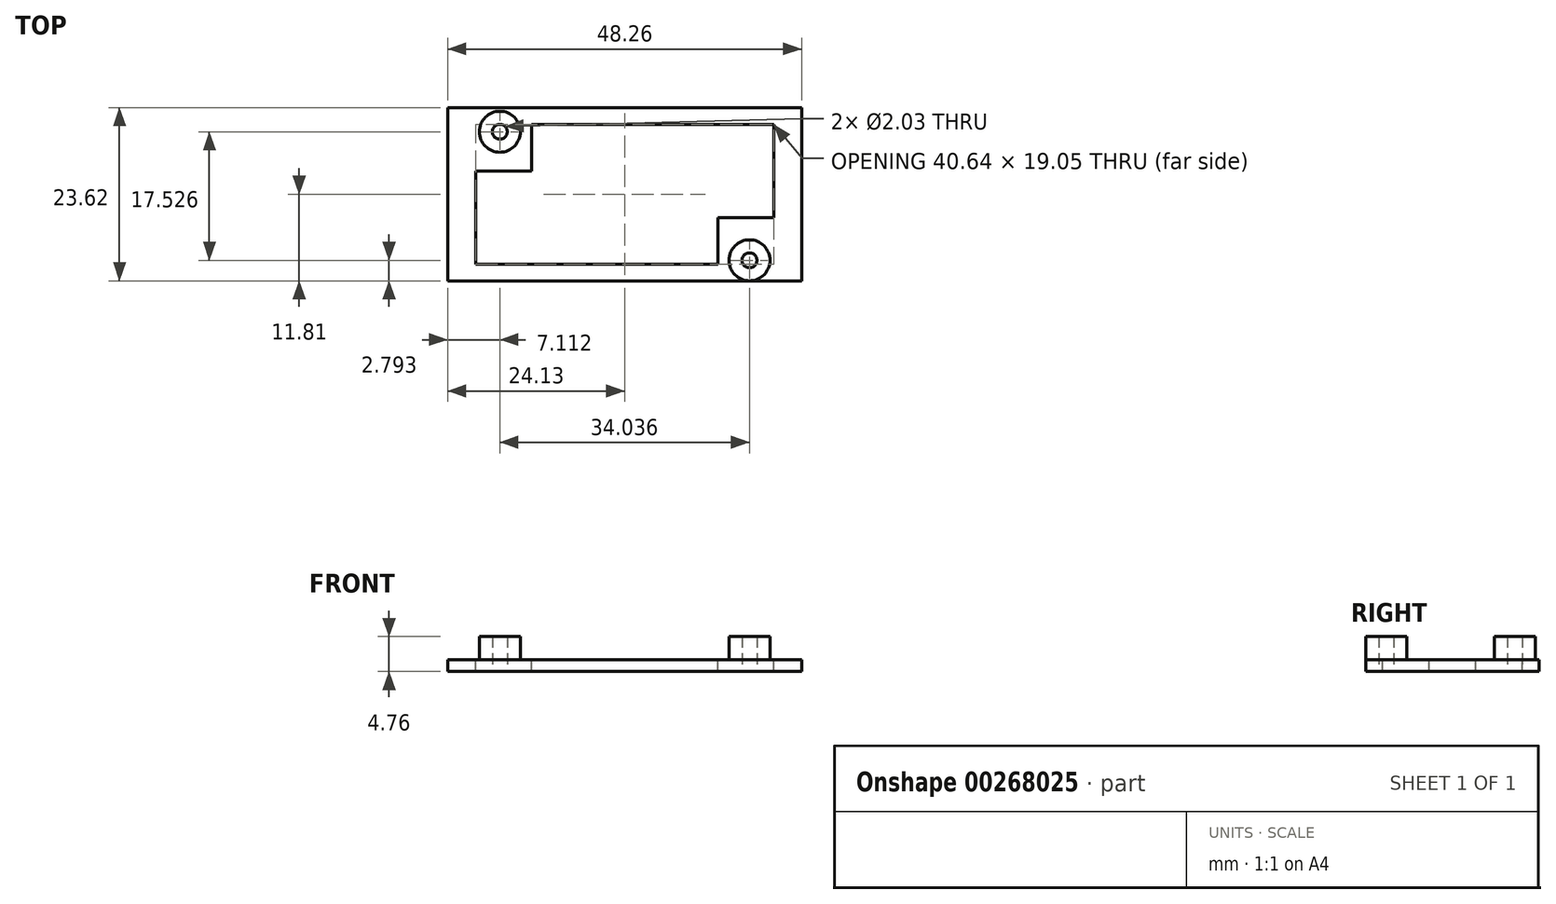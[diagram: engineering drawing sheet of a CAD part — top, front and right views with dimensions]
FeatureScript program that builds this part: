
annotation { "Feature Type Name" : "Feature", "Feature Type Description" : "" }
export const myFeature = defineFeature(function(context is Context, id is Id, definition is map)
    precondition{}
    {
        {
            var Q0;
            Q0=qCreatedBy(makeId("Top.planeOp"),FACE);
            var sketch = newSketch(context, id + "F0", { "sketchPlane" : qUnion([Q0])});
            skLineSegment(sketch, "E0.bottom", {"start": v(24.13, 11.81) * mm, "end": v(-24.13, 11.81) * mm});
            skLineSegment(sketch, "E0.top", {"start": v(24.13, -11.81) * mm, "end": v(-24.13, -11.81) * mm});
            skLineSegment(sketch, "E0.left", {"start": v(24.13, 11.81) * mm, "end": v(24.13, -11.81) * mm});
            skLineSegment(sketch, "E0.right", {"start": v(-24.13, 11.81) * mm, "end": v(-24.13, -11.81) * mm});
            skPoint(sketch, "E0.middle", {"position": v(0, 0) * mm});
            skSolve(sketch);
        }
        {
            var Q0;
            Q0=makeQuery(id+"F0.imprint","IMPRINT",FACE,{"disambiguationData":[TD([[makeQuery(id+"F0.imprint","IMPRINT",EDGE,{"derivedFrom":sQuery(id+"F0.wireOp",EDGE,"E0.bottom")}),1.0]])]});
            extrude(context, id + "F1", {"entities" : qUnion([Q0]), "depth" : 1.59 * mm});
        }
        {
            var Q0;
            Q0=makeQuery(id+"F1.opExtrude","CAP_FACE",FACE,{"disambiguationData":[OSD([sQuery(id+"F0.wireOp",EDGE,"E0.bottom"),sQuery(id+"F0.wireOp",EDGE,"E0.top"),sQuery(id+"F0.wireOp",EDGE,"E0.left"),sQuery(id+"F0.wireOp",EDGE,"E0.right")])],"isStart":false});
            var sketch = newSketch(context, id + "F2", { "sketchPlane" : qUnion([Q0])});
            skLineSegment(sketch, "E1.bottom", {"start": v(17.02, -11.81) * mm, "end": v(24.13, -11.81) * mm, "construction": true});
            skLineSegment(sketch, "E1.top", {"start": v(17.02, -9.02) * mm, "end": v(24.13, -9.02) * mm, "construction": true});
            skLineSegment(sketch, "E1.left", {"start": v(17.02, -11.81) * mm, "end": v(17.02, -9.02) * mm, "construction": true});
            skLineSegment(sketch, "E1.right", {"start": v(24.13, -11.81) * mm, "end": v(24.13, -9.02) * mm, "construction": true});
            skCircle(sketch, "E2", {"center": v(17.02, -9.02) * mm, "radius": 1.02 * mm});
            skCircle(sketch, "E3", {"center": v(17.02, -9.02) * mm, "radius": 2.8 * mm});
            skLineSegment(sketch, "E4.bottom", {"start": v(17.02, -9.02) * mm, "end": v(-17.02, -9.02) * mm, "construction": true});
            skLineSegment(sketch, "E4.top", {"start": v(17.02, 8.5) * mm, "end": v(-17.02, 8.5) * mm, "construction": true});
            skLineSegment(sketch, "E4.left", {"start": v(17.02, -9.02) * mm, "end": v(17.02, 8.5) * mm, "construction": true});
            skLineSegment(sketch, "E4.right", {"start": v(-17.02, -9.02) * mm, "end": v(-17.02, 8.5) * mm, "construction": true});
            skCircle(sketch, "E5", {"center": v(-17.02, 8.5) * mm, "radius": 1.02 * mm});
            skCircle(sketch, "E6", {"center": v(-17.02, 8.5) * mm, "radius": 2.8 * mm});
            skLineSegment(sketch, "E7.bottom", {"start": v(24.13, -11.81) * mm, "end": v(-24.13, -11.81) * mm, "construction": true});
            skLineSegment(sketch, "E7.top", {"start": v(24.13, 11.81) * mm, "end": v(-24.13, 11.81) * mm, "construction": true});
            skLineSegment(sketch, "E7.left", {"start": v(24.13, -11.81) * mm, "end": v(24.13, 11.81) * mm, "construction": true});
            skLineSegment(sketch, "E7.right", {"start": v(-24.13, -11.81) * mm, "end": v(-24.13, 11.81) * mm, "construction": true});
            skLineSegment(sketch, "E8.top", {"start": v(24.13, 11.3) * mm, "end": v(-24.13, 11.3) * mm, "construction": true});
            skLineSegment(sketch, "E8.left", {"start": v(24.13, -11.81) * mm, "end": v(24.13, 11.3) * mm, "construction": true});
            skLineSegment(sketch, "E8.right", {"start": v(-24.13, -11.81) * mm, "end": v(-24.13, 11.3) * mm, "construction": true});
            skLineSegment(sketch, "E9.bottom", {"start": v(-17.02, 8.5) * mm, "end": v(-24.13, 8.5) * mm, "construction": true});
            skLineSegment(sketch, "E9.top", {"start": v(-17.02, 11.3) * mm, "end": v(-24.13, 11.3) * mm, "construction": true});
            skLineSegment(sketch, "E9.left", {"start": v(-17.02, 8.5) * mm, "end": v(-17.02, 11.3) * mm, "construction": true});
            skLineSegment(sketch, "E9.right", {"start": v(-24.13, 8.5) * mm, "end": v(-24.13, 11.3) * mm, "construction": true});
            skSolve(sketch);
        }
        {
            var Q0;
            Q0=makeQuery(id+"F2.imprint","IMPRINT",FACE,{"disambiguationData":[TD([[makeQuery(id+"F2.imprint","IMPRINT",EDGE,{"derivedFrom":sQuery(id+"F2.wireOp",EDGE,"E5")}),-1.0]])]});
            var Q1;
            Q1 = qSketchRegion(id + "F2", true);
            var Q2;
            Q2=makeQuery(id+"F2.imprint","IMPRINT",FACE,{"disambiguationData":[TD([[makeQuery(id+"F2.imprint","IMPRINT",EDGE,{"derivedFrom":sQuery(id+"F2.wireOp",EDGE,"E2")}),-1.0]])]});
            extrude(context, id + "F3", {"entities" : qUnion([Q0, Q1, Q2]), "operationType" : NewBodyOperationType.ADD, "depth" : 3.17 * mm});
        }
        {
            var Q0;
            Q0=makeQuery(id+"F2.imprint","IMPRINT",FACE,{"disambiguationData":[TD([[makeQuery(id+"F2.imprint","IMPRINT",EDGE,{"derivedFrom":sQuery(id+"F2.wireOp",EDGE,"E5")}),1.0]])]});
            var Q1;
            Q1=makeQuery(id+"F2.imprint","IMPRINT",FACE,{"disambiguationData":[TD([[makeQuery(id+"F2.imprint","IMPRINT",EDGE,{"derivedFrom":sQuery(id+"F2.wireOp",EDGE,"E2")}),1.0]])]});
            extrude(context, id + "F4", {"entities" : qUnion([Q0, Q1]), "operationType" : NewBodyOperationType.REMOVE, "oppositeDirection" : true, "depth" : 6.35 * mm});
        }
        {
            var Q0;
            {var subQ0=sQuery(id+"F0.wireOp",EDGE,"E0.left");var subQ1=sQuery(id+"F0.wireOp",EDGE,"E0.top");var subQ2=sQuery(id+"F0.wireOp",EDGE,"E0.right");var subQ3=sQuery(id+"F0.wireOp",EDGE,"E0.bottom");Q0=makeQuery(id+"F3.boolean.opBoolean","SPLIT",FACE,{"disambiguationData":[TD([makeQuery(id+"F1.opExtrude","SWEPT_FACE",FACE,{"disambiguationData":[OSD([subQ3])]})])],"derivedFrom":makeQuery(id+"F1.opExtrude","CAP_FACE",FACE,{"disambiguationData":[OSD([subQ3,subQ1,subQ0,subQ2])],"isStart":false})});}
            var sketch = newSketch(context, id + "F5", { "sketchPlane" : qUnion([Q0])});
            skLineSegment(sketch, "E10.bottom", {"start": v(12.7, -9.52) * mm, "end": v(-12.7, -9.53) * mm});
            skLineSegment(sketch, "E10.top", {"start": v(12.7, 9.53) * mm, "end": v(-12.7, 9.52) * mm});
            skLineSegment(sketch, "E10.left", {"start": v(12.7, -9.53) * mm, "end": v(12.7, 9.53) * mm});
            skLineSegment(sketch, "E10.right", {"start": v(-12.7, -9.53) * mm, "end": v(-12.7, 9.52) * mm});
            skPoint(sketch, "E10.middle", {"position": v(0, 0) * mm});
            skLineSegment(sketch, "E11.bottom", {"start": v(-12.7, -9.53) * mm, "end": v(-20.32, -9.53) * mm});
            skLineSegment(sketch, "E11.top", {"start": v(-12.7, 3.17) * mm, "end": v(-20.32, 3.17) * mm});
            skLineSegment(sketch, "E11.left", {"start": v(-12.7, -9.53) * mm, "end": v(-12.7, 3.17) * mm});
            skLineSegment(sketch, "E11.right", {"start": v(-20.32, -9.53) * mm, "end": v(-20.32, 3.17) * mm});
            skLineSegment(sketch, "E12.bottom", {"start": v(12.7, 9.53) * mm, "end": v(20.32, 9.53) * mm});
            skLineSegment(sketch, "E12.top", {"start": v(12.7, -3.18) * mm, "end": v(20.32, -3.18) * mm});
            skLineSegment(sketch, "E12.left", {"start": v(12.7, 9.53) * mm, "end": v(12.7, -3.18) * mm});
            skLineSegment(sketch, "E12.right", {"start": v(20.32, 9.53) * mm, "end": v(20.32, -3.18) * mm});
            skSolve(sketch);
        }
        {
            var Q0;
            Q0=makeQuery(id+"F5.imprint","IMPRINT",FACE,{"disambiguationData":[TD([[makeQuery(id+"F5.imprint","IMPRINT",EDGE,{"derivedFrom":sQuery(id+"F5.wireOp",EDGE,"E10.bottom")}),-1.0]])]});
            var Q1;
            Q1=makeQuery(id+"F5.imprint","IMPRINT",FACE,{"disambiguationData":[TD([[makeQuery(id+"F5.imprint","IMPRINT",EDGE,{"derivedFrom":sQuery(id+"F5.wireOp",EDGE,"E12.bottom")}),-1.0]])]});
            var Q2;
            Q2=makeQuery(id+"F5.imprint","IMPRINT",FACE,{"disambiguationData":[TD([[makeQuery(id+"F5.imprint","IMPRINT",EDGE,{"derivedFrom":sQuery(id+"F5.wireOp",EDGE,"E11.bottom")}),-1.0]])]});
            extrude(context, id + "F6", {"entities" : qUnion([Q0, Q1, Q2]), "operationType" : NewBodyOperationType.REMOVE, "oppositeDirection" : true, "depth" : 6.35 * mm});
        }
    });
